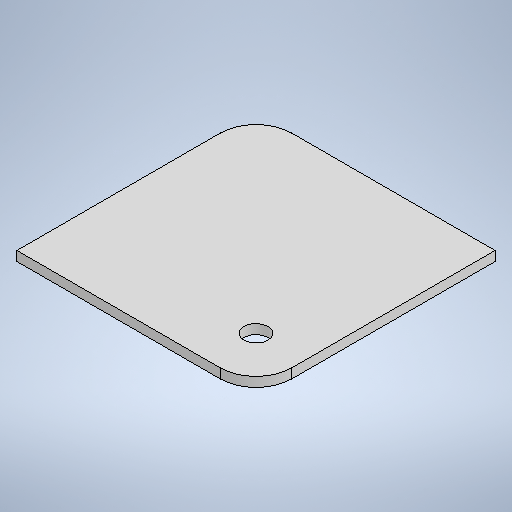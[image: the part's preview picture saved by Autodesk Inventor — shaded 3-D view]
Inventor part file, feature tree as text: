
AUTODESK INVENTOR PART (.ipt)
format: ipt  version: 2025 (Build 290162010, 162A)  size: 290,304 bytes
history: native  units: mm
features: other x2, sheet_metal_op x1, chamfer x1, sketch x1
ambient origin geometry x8: Origin, YZ Plane, XZ Plane, XY Plane, X Axis, Y Axis, Z Axis, Center Point
bodies: Body1 (feature_tree)
feature tree (5):
  sheet_metal_op  "Face3"
  chamfer  "Corner Round1"
  sketch  "Sketch1"  dims[d61=500.0mm d154=200.0mm d155=200.0mm d156=8.0mm d157=20.0mm d158=40.0mm d159=40.0mm d160=30.0mm d161=60.0mm]
  other  "Plate5"
  other  "Definition1"
